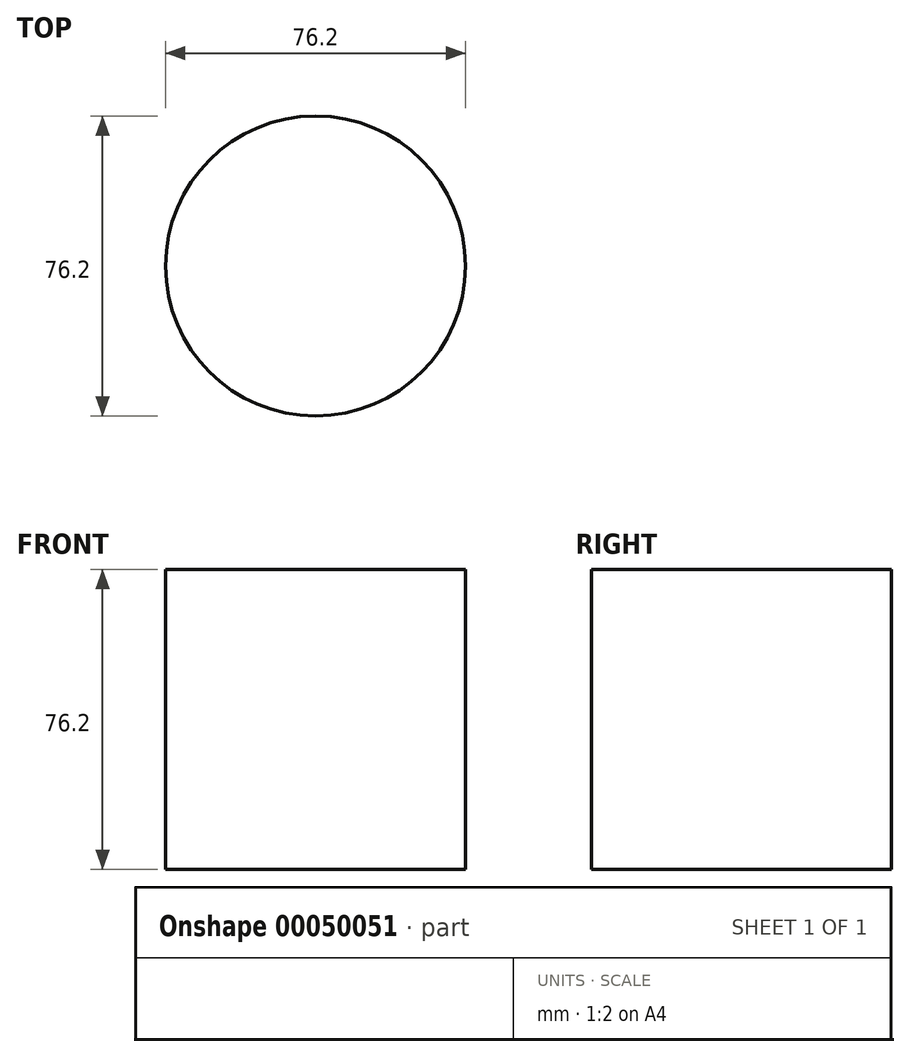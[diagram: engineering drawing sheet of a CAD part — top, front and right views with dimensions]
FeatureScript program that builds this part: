
annotation { "Feature Type Name" : "Feature", "Feature Type Description" : "" }
export const myFeature = defineFeature(function(context is Context, id is Id, definition is map)
    precondition{}
    {
        {
            var Q0;
            Q0=qCreatedBy(makeId("Top.planeOp"),FACE);
            var sketch = newSketch(context, id + "F0", { "sketchPlane" : qUnion([Q0])});
            skCircle(sketch, "E0", {"center": v(0, 0) * mm, "radius": 38.1 * mm});
            skSolve(sketch);
        }
        {
            var Q0;
            Q0 = qSketchRegion(id + "F0", true);
            extrude(context, id + "F1", {"entities" : qUnion([Q0]), "endBound" : BoundingType.SYMMETRIC, "depth" : 76.2 * mm});
        }
    });
